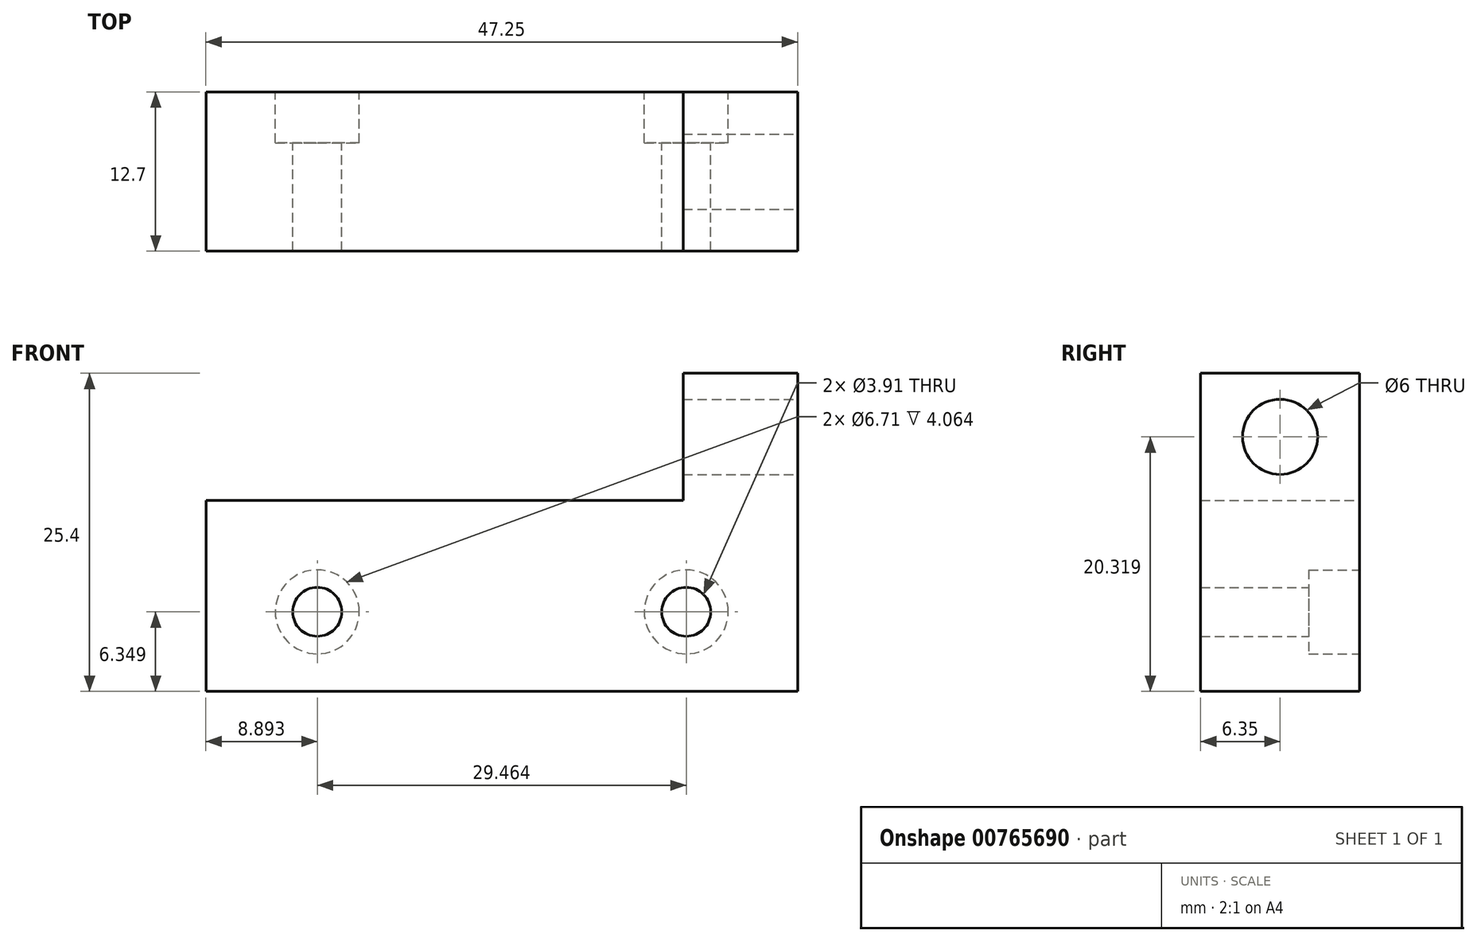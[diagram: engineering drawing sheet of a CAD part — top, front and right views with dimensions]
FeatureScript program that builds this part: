
annotation { "Feature Type Name" : "Feature", "Feature Type Description" : "" }
export const myFeature = defineFeature(function(context is Context, id is Id, definition is map)
    precondition{}
    {
        {
            var Q0;
            Q0=qCreatedBy(makeId("Front.planeOp"),FACE);
            var sketch = newSketch(context, id + "F0", { "sketchPlane" : qUnion([Q0])});
            skLineSegment(sketch, "E0.bottom", {"start": v(-44.07, 21.76) * mm, "end": v(3.18, 21.76) * mm});
            skLineSegment(sketch, "E0.top", {"start": v(-44.07, -3.64) * mm, "end": v(3.18, -3.64) * mm});
            skLineSegment(sketch, "E0.left", {"start": v(-44.07, 21.76) * mm, "end": v(-44.07, -3.64) * mm});
            skLineSegment(sketch, "E0.right", {"start": v(3.18, 21.76) * mm, "end": v(3.18, -3.64) * mm});
            skSolve(sketch);
        }
        {
            var Q0;
            Q0 = qSketchRegion(id + "F0", true);
            extrude(context, id + "F1", {"entities" : qUnion([Q0]), "depth" : 12.7 * mm, "offsetDistance" : 25.4 * mm});
        }
        {
            var Q0;
            Q0=makeQuery(id+"F1.opExtrude","CAP_FACE",FACE,{"disambiguationData":[OSD([sQuery(id+"F0.wireOp",EDGE,"E0.bottom"),sQuery(id+"F0.wireOp",EDGE,"E0.top"),sQuery(id+"F0.wireOp",EDGE,"E0.left"),sQuery(id+"F0.wireOp",EDGE,"E0.right")])],"isStart":true});
            var sketch = newSketch(context, id + "F2", { "sketchPlane" : qUnion([Q0])});
            skCircle(sketch, "E1", {"center": v(5.71, 2.7) * mm, "radius": 1.96 * mm});
            skCircle(sketch, "E2", {"center": v(35.18, 2.7) * mm, "radius": 1.96 * mm});
            skSolve(sketch);
        }
        {
            var Q0;
            Q0 = qSketchRegion(id + "F2", true);
            extrude(context, id + "F3", {"entities" : qUnion([Q0]), "operationType" : NewBodyOperationType.REMOVE, "endBound" : BoundingType.UP_TO_NEXT, "oppositeDirection" : true, "depth" : 25.4 * mm, "offsetDistance" : 25.4 * mm});
        }
        {
            var Q0;
            Q0=makeQuery(id+"F1.opExtrude","CAP_FACE",FACE,{"disambiguationData":[OSD([sQuery(id+"F0.wireOp",EDGE,"E0.bottom"),sQuery(id+"F0.wireOp",EDGE,"E0.top"),sQuery(id+"F0.wireOp",EDGE,"E0.left"),sQuery(id+"F0.wireOp",EDGE,"E0.right")])],"isStart":true});
            var sketch = newSketch(context, id + "F4", { "sketchPlane" : qUnion([Q0])});
            skCircle(sketch, "E3", {"center": v(5.71, 2.7) * mm, "radius": 3.35 * mm});
            skCircle(sketch, "E4", {"center": v(35.18, 2.7) * mm, "radius": 3.35 * mm});
            skSolve(sketch);
        }
        {
            var Q0;
            Q0 = qSketchRegion(id + "F4", true);
            extrude(context, id + "F5", {"entities" : qUnion([Q0]), "operationType" : NewBodyOperationType.REMOVE, "oppositeDirection" : true, "depth" : 4.06 * mm, "offsetDistance" : 25.4 * mm});
        }
        {
            var Q0;
            Q0=makeQuery(id+"F1.opExtrude","SWEPT_FACE",FACE,{"disambiguationData":[OSD([sQuery(id+"F0.wireOp",EDGE,"E0.right")])]});
            var sketch = newSketch(context, id + "F6", { "sketchPlane" : qUnion([Q0])});
            skLineSegment(sketch, "E5", {"start": v(-6.35, 21.76) * mm, "end": v(-6.35, 16.68) * mm});
            skCircle(sketch, "E6", {"center": v(-6.35, 16.68) * mm, "radius": 3 * mm});
            skSolve(sketch);
        }
        {
            var Q0;
            Q0 = qSketchRegion(id + "F6", true);
            extrude(context, id + "F7", {"entities" : qUnion([Q0]), "operationType" : NewBodyOperationType.REMOVE, "oppositeDirection" : true, "depth" : 25.4 * mm, "offsetDistance" : 25.4 * mm});
        }
        {
            var Q0;
            Q0=makeQuery(id+"F1.opExtrude","CAP_FACE",FACE,{"disambiguationData":[OSD([sQuery(id+"F0.wireOp",EDGE,"E0.bottom"),sQuery(id+"F0.wireOp",EDGE,"E0.top"),sQuery(id+"F0.wireOp",EDGE,"E0.left"),sQuery(id+"F0.wireOp",EDGE,"E0.right")])],"isStart":true});
            var sketch = newSketch(context, id + "F8", { "sketchPlane" : qUnion([Q0])});
            skLineSegment(sketch, "E7.bottom", {"start": v(44.07, 21.76) * mm, "end": v(5.97, 21.76) * mm});
            skLineSegment(sketch, "E7.top", {"start": v(44.07, 11.6) * mm, "end": v(5.97, 11.6) * mm});
            skLineSegment(sketch, "E7.left", {"start": v(44.07, 21.76) * mm, "end": v(44.07, 11.6) * mm});
            skLineSegment(sketch, "E7.right", {"start": v(5.97, 21.76) * mm, "end": v(5.97, 11.6) * mm});
            skSolve(sketch);
        }
        {
            var Q0;
            Q0 = qSketchRegion(id + "F8", true);
            extrude(context, id + "F9", {"entities" : qUnion([Q0]), "operationType" : NewBodyOperationType.REMOVE, "endBound" : BoundingType.UP_TO_NEXT, "oppositeDirection" : true, "depth" : 25.4 * mm, "offsetDistance" : 25.4 * mm});
        }
    });
